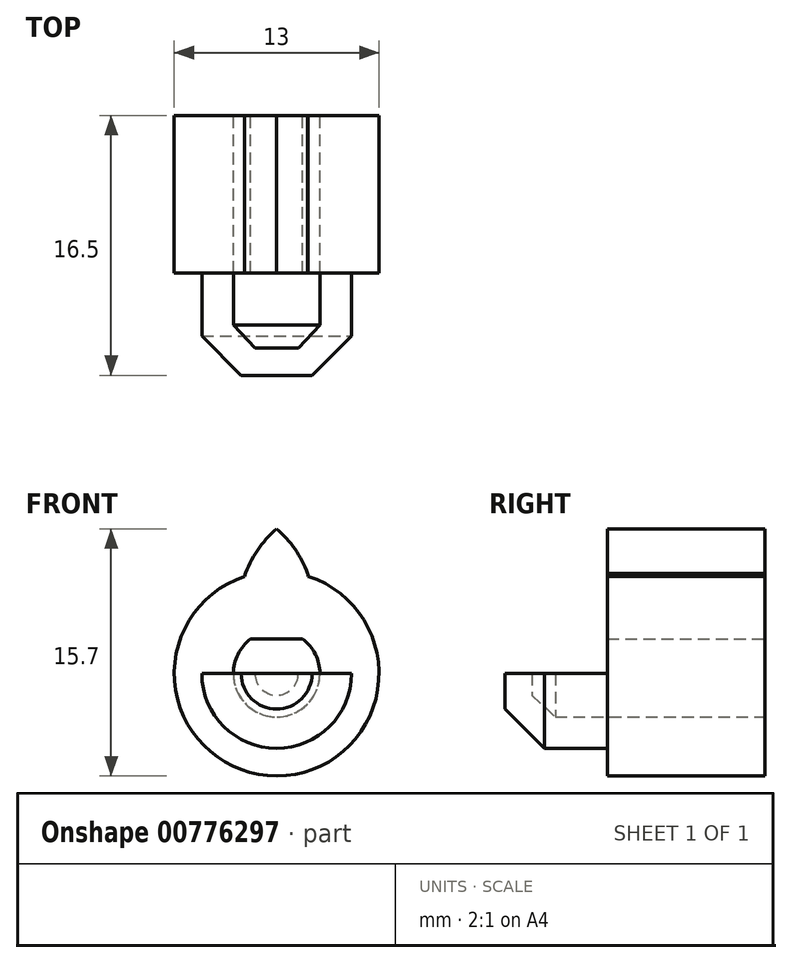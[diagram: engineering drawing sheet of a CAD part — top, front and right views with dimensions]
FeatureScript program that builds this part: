
annotation { "Feature Type Name" : "Feature", "Feature Type Description" : "" }
export const myFeature = defineFeature(function(context is Context, id is Id, definition is map)
    precondition{}
    {
        {
            var Q0;
            Q0=qCreatedBy(makeId("Top.planeOp"),FACE);
            var sketch = newSketch(context, id + "F0", { "sketchPlane" : qUnion([Q0])});
            skLineSegment(sketch, "E0.bottom", {"start": v(0, 0) * mm, "end": v(-6.5, 0) * mm});
            skLineSegment(sketch, "E0.top", {"start": v(0, 10) * mm, "end": v(-6.5, 10) * mm});
            skLineSegment(sketch, "E0.left", {"start": v(0, 0) * mm, "end": v(0, 10) * mm});
            skLineSegment(sketch, "E0.right", {"start": v(-6.5, 0) * mm, "end": v(-6.5, 10) * mm});
            skSolve(sketch);
        }
        {
            var Q0;
            Q0=makeQuery(id+"F0.imprint","IMPRINT",FACE,{"disambiguationData":[TD([[makeQuery(id+"F0.imprint","IMPRINT",EDGE,{"derivedFrom":sQuery(id+"F0.wireOp",EDGE,"E0.bottom")}),-1.0]])]});
            var Q1;
            Q1=sQuery(id+"F0.wireOp",EDGE,"E0.left");
            revolve(context, id + "F1", {"surfaceOperationType" : NewSurfaceOperationType.NEW, "entities" : qUnion([Q0]), "axis" : qUnion([Q1]), "revolveType" : RevolveType.FULL});
        }
        {
            var Q0;
            Q0=makeQuery(id+"F1.opRevolve","SWEPT_FACE",FACE,{"disambiguationData":[OSD([sQuery(id+"F0.wireOp",EDGE,"E0.top")])]});
            var sketch = newSketch(context, id + "F2", { "sketchPlane" : qUnion([Q0])});
            skArc(sketch, "E1", {"start": v(-1.65, 2.2) * mm, "mid": v(0, -2.75) * mm, "end": v(1.65, 2.2) * mm});
            skLineSegment(sketch, "E2", {"start": v(1.65, 2.2) * mm, "end": v(-1.65, 2.2) * mm});
            skSolve(sketch);
        }
        {
            var Q0;
            Q0=makeQuery(id+"F2.imprint","IMPRINT",FACE,{"disambiguationData":[TD([[makeQuery(id+"F2.imprint","IMPRINT",EDGE,{"derivedFrom":sQuery(id+"F2.wireOp",EDGE,"E1")}),1.0]])]});
            var Q1;
            Q1 = qSketchRegion(id + "F4", true);
            extrude(context, id + "F3", {"entities" : qUnion([Q0, Q1]), "operationType" : NewBodyOperationType.REMOVE, "oppositeDirection" : true, "depth" : 25 * mm, "offsetDistance" : 25 * mm});
        }
        {
            var Q0;
            Q0=makeQuery(id+"F1.opRevolve","SWEPT_FACE",FACE,{"disambiguationData":[OSD([sQuery(id+"F0.wireOp",EDGE,"E0.top")])]});
            var sketch = newSketch(context, id + "F4", { "sketchPlane" : qUnion([Q0])});
            skCircle(sketch, "E3", {"center": v(0, 0) * mm, "radius": 9.2 * mm, "construction": true});
            skLineSegment(sketch, "E4", {"start": v(0, 9.2) * mm, "end": v(-2, 6.18) * mm, "construction": true});
            skLineSegment(sketch, "E5.MirrorCS", {"start": v(0, 9.2) * mm, "end": v(2, 6.18) * mm, "construction": true});
            skArc(sketch, "E6", {"start": v(2.04, 6.17) * mm, "mid": v(1.23, 7.83) * mm, "end": v(0, 9.2) * mm});
            skArc(sketch, "E7.MirrorCS", {"start": v(-2, 6.18) * mm, "mid": v(-1.99, 6.27) * mm, "end": v(-1.97, 6.36) * mm});
            skPoint(sketch, "E8.orphan", {"position": v(0, 9.2) * mm});
            skLineSegment(sketch, "E9", {"start": v(0, -9.54) * mm, "end": v(0, 12.58) * mm, "construction": true});
            skLineSegment(sketch, "E10", {"start": v(0, 0) * mm, "end": v(-4.17, 12.84) * mm, "construction": true});
            skLineSegment(sketch, "E11", {"start": v(0, 0) * mm, "end": v(4.47, 13.77) * mm, "construction": true});
            skArc(sketch, "E12.MirrorCS", {"start": v(-2.04, 6.17) * mm, "mid": v(-1.23, 7.83) * mm, "end": v(0, 9.2) * mm});
            skSolve(sketch);
        }
        {
            var Q0;
            {var subQ0=sQuery(id+"F4.wireOp",EDGE,"E6");Q0=makeQuery(id+"F4.imprint","IMPRINT",FACE,{"disambiguationData":[TD([[makeQuery(id+"F4.imprint","IMPRINT",EDGE,{"derivedFrom":subQ0}),1.0]])]});}
            extrude(context, id + "F5", {"entities" : qUnion([Q0]), "operationType" : NewBodyOperationType.ADD, "oppositeDirection" : true, "depth" : 10 * mm, "offsetDistance" : 25 * mm});
        }
        {
            var Q0;
            {var subQ0=sQuery(id+"F4.wireOp",EDGE,"E12.MirrorCS");var subQ1=sQuery(id+"F4.wireOp",EDGE,"E7.MirrorCS");var subQ2=sQuery(id+"F4.wireOp",EDGE,"E6");var subQ3=sQuery(id+"F0.wireOp",EDGE,"E0.right");var subQ4=sQuery(id+"F0.wireOp",EDGE,"E0.top");Q0=makeQuery(id+"F2QCRiW7zeUK0pj_1.9.F5.boolean.opBoolean","MERGE",FACE,{"derivedFrom":[makeQuery(id+"F2QCRiW7zeUK0pj_1.8.F5.boolean.opBoolean","MERGE",FACE,{"derivedFrom":[makeQuery(id+"F2QCRiW7zeUK0pj_1.7.F5.boolean.opBoolean","MERGE",FACE,{"derivedFrom":[makeQuery(id+"F2QCRiW7zeUK0pj_1.6.F5.boolean.opBoolean","MERGE",FACE,{"derivedFrom":[makeQuery(id+"F2QCRiW7zeUK0pj_1.5.F5.boolean.opBoolean","MERGE",FACE,{"derivedFrom":[makeQuery(id+"F2QCRiW7zeUK0pj_1.4.F5.boolean.opBoolean","MERGE",FACE,{"derivedFrom":[makeQuery(id+"F2QCRiW7zeUK0pj_1.3.F5.boolean.opBoolean","MERGE",FACE,{"derivedFrom":[makeQuery(id+"F2QCRiW7zeUK0pj_1.2.F5.boolean.opBoolean","MERGE",FACE,{"derivedFrom":[makeQuery(id+"F2QCRiW7zeUK0pj_1.1.F5.boolean.opBoolean","MERGE",FACE,{"derivedFrom":[makeQuery(id+"F5.boolean.opBoolean","MERGE",FACE,{"derivedFrom":[makeQuery(id+"F1.opRevolve","SWEPT_FACE",FACE,{"disambiguationData":[OSD([sQuery(id+"F0.wireOp",EDGE,"E0.bottom")])]}),makeQuery(id+"F5.opExtrude","CAP_FACE",FACE,{"disambiguationData":[OSD([subQ4,subQ3,subQ2,subQ1,subQ0])],"isStart":false})]}),makeQuery(id+"F2QCRiW7zeUK0pj_1.1.F5.opExtrude","CAP_FACE",FACE,{"disambiguationData":[OSD([subQ4,subQ3,subQ2,subQ1,subQ0])],"isStart":false})]}),makeQuery(id+"F2QCRiW7zeUK0pj_1.2.F5.opExtrude","CAP_FACE",FACE,{"disambiguationData":[OSD([subQ4,subQ3,subQ2,subQ1,subQ0])],"isStart":false})]}),makeQuery(id+"F2QCRiW7zeUK0pj_1.3.F5.opExtrude","CAP_FACE",FACE,{"disambiguationData":[OSD([subQ4,subQ3,subQ2,subQ1,subQ0])],"isStart":false})]}),makeQuery(id+"F2QCRiW7zeUK0pj_1.4.F5.opExtrude","CAP_FACE",FACE,{"disambiguationData":[OSD([subQ4,subQ3,subQ2,subQ1,subQ0])],"isStart":false})]}),makeQuery(id+"F2QCRiW7zeUK0pj_1.5.F5.opExtrude","CAP_FACE",FACE,{"disambiguationData":[OSD([subQ4,subQ3,subQ2,subQ1,subQ0])],"isStart":false})]}),makeQuery(id+"F2QCRiW7zeUK0pj_1.6.F5.opExtrude","CAP_FACE",FACE,{"disambiguationData":[OSD([subQ4,subQ3,subQ2,subQ1,subQ0])],"isStart":false})]}),makeQuery(id+"F2QCRiW7zeUK0pj_1.7.F5.opExtrude","CAP_FACE",FACE,{"disambiguationData":[OSD([subQ4,subQ3,subQ2,subQ1,subQ0])],"isStart":false})]}),makeQuery(id+"F2QCRiW7zeUK0pj_1.8.F5.opExtrude","CAP_FACE",FACE,{"disambiguationData":[OSD([subQ4,subQ3,subQ2,subQ1,subQ0])],"isStart":false})]}),makeQuery(id+"F2QCRiW7zeUK0pj_1.9.F5.opExtrude","CAP_FACE",FACE,{"disambiguationData":[OSD([subQ4,subQ3,subQ2,subQ1,subQ0])],"isStart":false})]});}
            var sketch = newSketch(context, id + "F6", { "sketchPlane" : qUnion([Q0])});
            skLineSegment(sketch, "E13", {"start": v(0, 9.2) * mm, "end": v(0, -8.7) * mm, "construction": true});
            skPoint(sketch, "E14", {"position": v(-4.75, 0) * mm});
            skPoint(sketch, "E15", {"position": v(4.75, 0) * mm});
            skPoint(sketch, "E16", {"position": v(0, 4.75) * mm});
            skPoint(sketch, "E17", {"position": v(0, -4.75) * mm});
            skPoint(sketch, "E18", {"position": v(0, 0) * mm});
            skArc(sketch, "E19", {"start": v(-4.75, 0) * mm, "mid": v(0, -4.75) * mm, "end": v(4.75, 0) * mm});
            skLineSegment(sketch, "E20", {"start": v(-4.75, 0) * mm, "end": v(4.75, 0) * mm});
            skSolve(sketch);
        }
        {
            var Q0;
            {var subQ0=sQuery(id+"F6.wireOp",EDGE,"E19");Q0=makeQuery(id+"F6.imprint","IMPRINT",FACE,{"disambiguationData":[TD([[makeQuery(id+"F6.imprint","IMPRINT",EDGE,{"derivedFrom":subQ0}),1.0]])]});}
            var Q1;
            {var subQ0=sQuery(id+"F6.wireOp",EDGE,"E20");var subQ1=makeQuery(id+"F3.boolean.opBoolean","INTERSECT",EDGE,{"derivedFrom":[makeQuery(id+"F1.opRevolve","SWEPT_FACE",FACE,{"disambiguationData":[OSD([sQuery(id+"F0.wireOp",EDGE,"E0.bottom")])]}),makeQuery(id+"F3.opExtrude","SWEPT_FACE",FACE,{"disambiguationData":[OSD([sQuery(id+"F2.wireOp",EDGE,"E1")])]})]});var subQ2=makeQuery(id+"F6.imprint","INTERSECT",VERTEX,{"disambiguationData":[OD(0.0)],"derivedFrom":[subQ1,subQ0]});Q1=makeQuery(id+"F6.imprint","IMPRINT",FACE,{"disambiguationData":[TD([[makeQuery(id+"F6.imprint","IMPRINT",EDGE,{"disambiguationData":[TD([[subQ2,-1.0]])],"derivedFrom":subQ0}),-1.0]])]});}
            extrude(context, id + "F7", {"entities" : qUnion([Q0, Q1]), "operationType" : NewBodyOperationType.ADD, "depth" : 6.5 * mm, "offsetDistance" : 25 * mm});
        }
        {
            var Q0;
            Q0=makeQuery(id+"F7.opExtrude","SWEPT_FACE",FACE,{"disambiguationData":[OSD([sQuery(id+"F6.wireOp",EDGE,"E20")])]});
            var sketch = newSketch(context, id + "F8", { "sketchPlane" : qUnion([Q0])});
            skLineSegment(sketch, "E21", {"start": v(0, 0) * mm, "end": v(0, -6.5) * mm, "construction": true});
            skPoint(sketch, "E22", {"position": v(0, -4.78) * mm});
            skLineSegment(sketch, "E23", {"start": v(0, 0) * mm, "end": v(-2.75, 0) * mm});
            skLineSegment(sketch, "E24", {"start": v(0, -1.83) * mm, "end": v(0, -4.78) * mm});
            skLineSegment(sketch, "E25", {"start": v(-2.75, 0) * mm, "end": v(-2.75, -3.3) * mm});
            skPoint(sketch, "E25.endSnap0", {"position": v(0, -3.3) * mm});
            skLineSegment(sketch, "E26", {"start": v(-2.75, -3.3) * mm, "end": v(-1.37, -4.78) * mm});
            skPoint(sketch, "E26.endSnap0", {"position": v(-1.38, 0) * mm});
            skLineSegment(sketch, "E27", {"start": v(-1.38, -4.77) * mm, "end": v(0, -4.77) * mm});
            skLineSegment(sketch, "E28", {"start": v(0, -3.3) * mm, "end": v(0, -1.33) * mm});
            skLineSegment(sketch, "E29", {"start": v(0, -3.3) * mm, "end": v(0, 0) * mm});
            skSolve(sketch);
        }
        {
            var Q0;
            Q0=makeQuery(id+"F7.opExtrude","CAP_EDGE",EDGE,{"disambiguationData":[OSD([sQuery(id+"F6.wireOp",EDGE,"E19")])],"isStart":false});
            chamfer(context, id + "F9", {"entities" : qUnion([Q0]), "width" : 2.5 * mm, "tangentPropagation" : true});
        }
        {
            var Q0;
            Q0=makeQuery(id+"F8.imprint","IMPRINT",FACE,{"disambiguationData":[TD([[makeQuery(id+"F8.imprint","IMPRINT",EDGE,{"derivedFrom":sQuery(id+"F8.wireOp",EDGE,"E23")}),-1.0]])]});
            var Q1;
            Q1=sQuery(id+"F8.wireOp",EDGE,"E24");
            revolve(context, id + "F10", {"operationType" : NewBodyOperationType.REMOVE, "surfaceOperationType" : NewSurfaceOperationType.NEW, "entities" : qUnion([Q0]), "axis" : qUnion([Q1]), "revolveType" : RevolveType.FULL, "oppositeDirection" : true});
        }
    });
